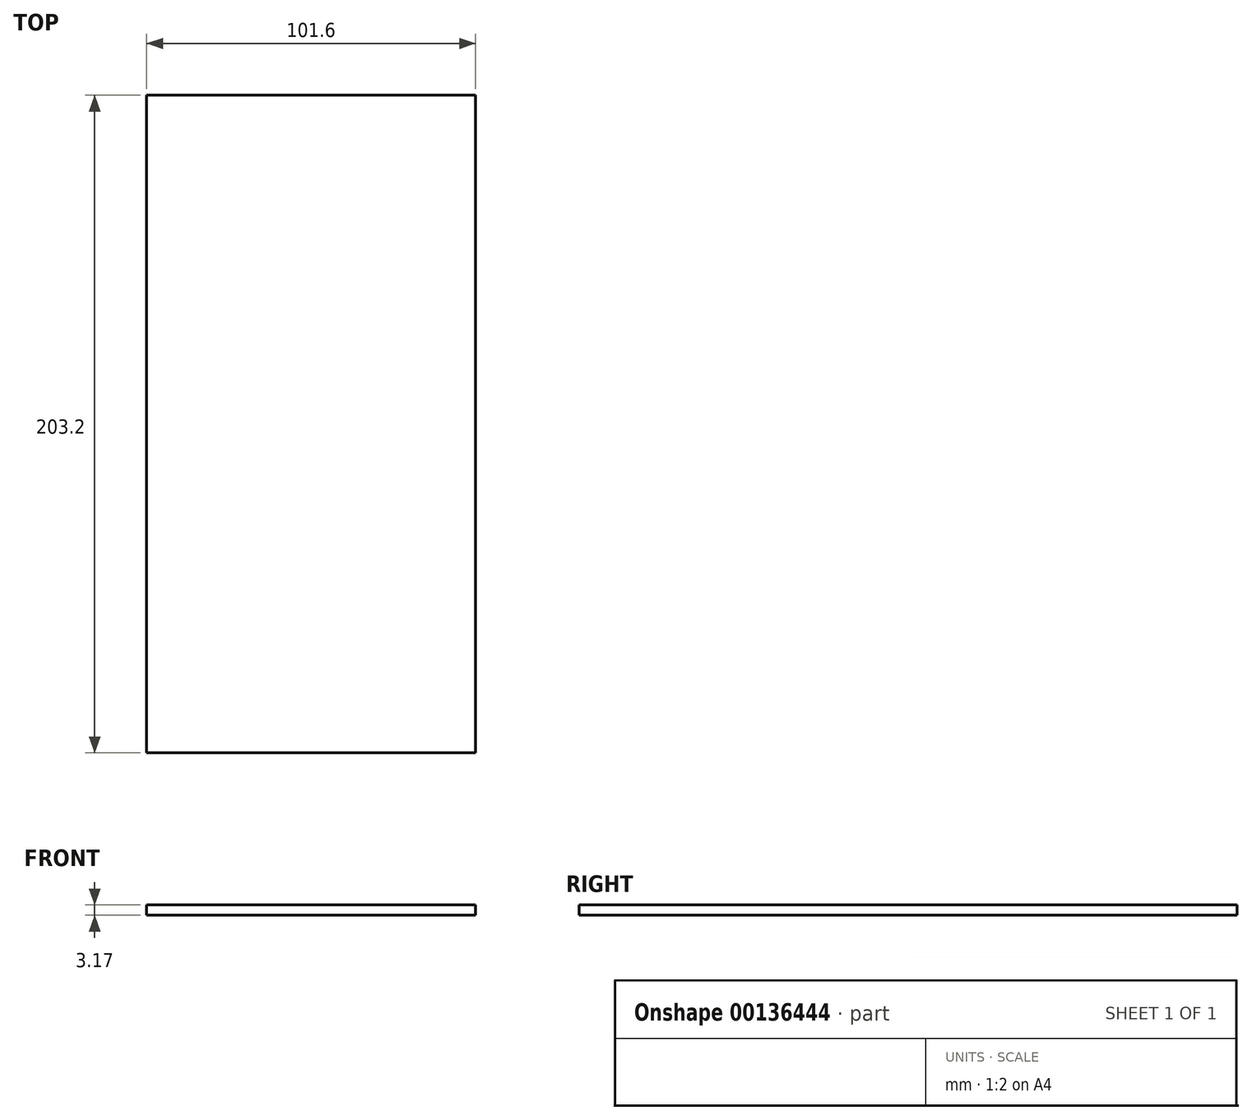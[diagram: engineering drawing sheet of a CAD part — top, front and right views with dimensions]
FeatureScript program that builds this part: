
annotation { "Feature Type Name" : "Feature", "Feature Type Description" : "" }
export const myFeature = defineFeature(function(context is Context, id is Id, definition is map)
    precondition{}
    {
        {
            var Q0;
            Q0=qCreatedBy(makeId("Top.planeOp"),FACE);
            var sketch = newSketch(context, id + "F0", { "sketchPlane" : qUnion([Q0])});
            skLineSegment(sketch, "E0.bottom", {"start": v(0, 0) * mm, "end": v(101.6, 0) * mm});
            skLineSegment(sketch, "E0.top", {"start": v(0, 203.2) * mm, "end": v(101.6, 203.2) * mm});
            skLineSegment(sketch, "E0.left", {"start": v(0, 0) * mm, "end": v(0, 203.2) * mm});
            skLineSegment(sketch, "E0.right", {"start": v(101.6, 0) * mm, "end": v(101.6, 203.2) * mm});
            skSolve(sketch);
        }
        {
            var Q0;
            Q0=makeQuery(id+"F0.imprint","IMPRINT",FACE,{"disambiguationData":[TD([[makeQuery(id+"F0.imprint","IMPRINT",EDGE,{"derivedFrom":sQuery(id+"F0.wireOp",EDGE,"E0.bottom")}),1.0]])]});
            extrude(context, id + "F1", {"entities" : qUnion([Q0]), "depth" : 3.17 * mm});
        }
    });
